# Revit family: Hager-UNIVERS-Surface_mounted-IP44-With_Cover-Without_DIN-Hosted-AT-de
name_source: partatom
category: Electrical Equipment
units: mm (PartAtom-declared; Revit-internal decimal feet)

## family parameters
Cut with Voids When Loaded = No
Host = Face
Maintain Annotation Orientation = Yes
Panel Configuration = Two Columns, Circuits Across
Part Type = Panelboard
Room Calculation Point = No
Round Connector Dimension = Use Diameter
Shared = No

## types (20) — shared parameters
BC_MODEL_ID = 1539154
BC_OBJECT_ID = 512277
BC_OBJECT_VERSION = #6
Code hager = ADD-EC000214_EU
EF000003 - Montageart = Aufputz
EF000007 - Farbe = weiß
EF000024 - UV-beständig = No
EF000049 - Tiefe = 161 mm  [stored 0.528215 ft]
EF000116 - RAL-Nummer = 9010
EF000118 - Mit Montageplatte = No
EF001062 - EMV-Ausführung = No
EF001088 - Anbaumöglichkeit = Yes
EF001134 - DIN-Schiene = No
EF004462 - Art der Schließung = sonstige
EF005474 - Schutzart (IP) = IP44
EF006244 - Transparenter Deckel/Tür = No
EF006306 - Mit Schloss = No
EF009212 - Ausführung Deckel = mit Ausschnitt
EF015776 - Erdungsklemmenblock = No
EF015777 - Neutralleiterklemmenblock = No
EF015941 - Signaldurchlassende Tür = No
ETIM class code = EC000214
ETIM class name = Small distribution board
HG000002-Mit tür = Yes
HG000003-Bereich = UNIVERS
HG000005-Dicke = 2 mm  [stored 0.00656168 ft]
HG000006-Unterputz = No
HG000011-Leere Reihen von unten = No
HG000012-Türschwenkwinkel = 90.00°
HG000013-Tür links = No
HG000014-Tür rechts = Yes
HG000015-Sichtbarkeit der Türöffnung = Yes
HG000016-3D-Türsichtbarkeit = Yes
HG000017-Distanz zwischen den Polen = 18 mm  [stored 0.0590551 ft]
HG000060-RAL-number = 9010
HG000099-Onfly Template ID-de-AT = 507532
Manufacturer = Hager
Name = UNIVERS-Surface_mounted-IP44-With_Cover-Without_DIN-AT
Name BIM&CO = Electricity
Name hager = ADD_Enclosures_EC000214
Uniformat = Low Tension Service & Dist.
Uniformat code = D501001
zero-valued in all types: Default Elevation, EF001131 - Innentiefe, HG000007-Anzahl der leeren Spalten, HG000008-Anzahl der leeren Reihen

## per-type parameters (varying)
| type | BC_VARIANT_ID | EF000008 - Breite | EF000040 - Höhe | EF000218 - Einbautiefe | EF000266 - Anzahl der Reihen | EF000332 - Einbauhöhe | EF000846 - Einbaubreite | EF002950 - Breite in Teilungseinheiten | HG000001-Anzahl der Spalten | HG000004-Herstellerreferenz | HG000009-Doppelflügeligen Tür | HG000010-Asymmetrische Türen | HGEF000266-Anzahl der Reihen | HGEF0002950-Breite in Teilungseinheiten |
| UNIVERS-Surface_mounted_W300_H500_D161_12_Modular_Spacing-FWQ31P | 1169533 | 300 mm | 500 mm  [stored 1.64042 ft] | 0 mm  [stored 0 ft] | 3 | 500 mm  [stored 1.64042 ft] | 300 mm | 12 | 1 | FWQ31P | No | No | 3 | 12 |
| UNIVERS-Surface_mounted_W550_H500_D161_24_Modular_Spacing-FWQ32P | 1169534 | 550 mm | 500 mm  [stored 1.64042 ft] | 161 mm  [stored 0.528215 ft] | 3 | 500 mm  [stored 1.64042 ft] | 550 mm | 24 | 2 | FWQ32P | No | No | 3 | 24 |
| UNIVERS-Surface_mounted_W800_H500_D161_36_Modular_Spacing-FWQ33P | 1169537 | 800 mm  [stored 2.62467 ft] | 500 mm  [stored 1.64042 ft] | 0 mm  [stored 0 ft] | 3 | 500 mm  [stored 1.64042 ft] | 800 mm  [stored 2.62467 ft] | 36 | 3 | FWQ33P | Yes | Yes | 3 | 36 |
| UNIVERS-Surface_mounted_W1050_H500_D161_48_Modular_Spacing-FWQ34P | 1169542 | 1050 mm | 500 mm  [stored 1.64042 ft] | 0 mm  [stored 0 ft] | 3 | 500 mm  [stored 1.64042 ft] | 1050 mm | 48 | 4 | FWQ34P | Yes | No | 3 | 48 |
| UNIVERS-Surface_mounted_W300_H650_D161_12_Modular_Spacing-FWQ41P | 1169548 | 300 mm | 650 mm  [stored 2.13255 ft] | 0 mm  [stored 0 ft] | 4 | 650 mm  [stored 2.13255 ft] | 300 mm | 12 | 1 | FWQ41P | No | No | 4 | 12 |
| UNIVERS-Surface_mounted_W550_H650_D161_24_Modular_Spacing-FWQ42P | 1169552 | 550 mm | 650 mm  [stored 2.13255 ft] | 0 mm  [stored 0 ft] | 4 | 650 mm  [stored 2.13255 ft] | 550 mm | 24 | 2 | FWQ42P | No | No | 4 | 24 |
| UNIVERS-Surface_mounted_W800_H650_D161_36_Modular_Spacing-FWQ43P | 1169555 | 800 mm  [stored 2.62467 ft] | 650 mm  [stored 2.13255 ft] | 0 mm  [stored 0 ft] | 4 | 650 mm  [stored 2.13255 ft] | 800 mm  [stored 2.62467 ft] | 36 | 3 | FWQ43P | Yes | Yes | 4 | 36 |
| UNIVERS-Surface_mounted_W1050_H650_D161_48_Modular_Spacing-FWQ44P | 1169557 | 1050 mm | 650 mm  [stored 2.13255 ft] | 0 mm  [stored 0 ft] | 4 | 650 mm  [stored 2.13255 ft] | 1050 mm | 48 | 4 | FWQ44P | Yes | No | 4 | 48 |
| UNIVERS-Surface_mounted_W300_H800_D161_12_Modular_Spacing-FWQ51P | 1169561 | 300 mm | 800 mm  [stored 2.62467 ft] | 0 mm  [stored 0 ft] | 5 | 800 mm  [stored 2.62467 ft] | 300 mm | 12 | 1 | FWQ51P | No | No | 5 | 12 |
| UNIVERS-Surface_mounted_W550_H800_D161_24_Modular_Spacing-FWQ52P | 1169563 | 550 mm | 800 mm  [stored 2.62467 ft] | 161 mm  [stored 0.528215 ft] | 5 | 800 mm  [stored 2.62467 ft] | 550 mm | 24 | 2 | FWQ52P | No | No | 5 | 24 |
| UNIVERS-Surface_mounted_W800_H800_D161_36_Modular_Spacing-FWQ53P | 1169566 | 800 mm  [stored 2.62467 ft] | 800 mm  [stored 2.62467 ft] | 0 mm  [stored 0 ft] | 5 | 800 mm  [stored 2.62467 ft] | 800 mm  [stored 2.62467 ft] | 36 | 3 | FWQ53P | Yes | Yes | 5 | 36 |
| UNIVERS-Surface_mounted_W1050_H800_D161_48_Modular_Spacing-FWQ54P | 1169570 | 1050 mm | 800 mm  [stored 2.62467 ft] | 0 mm  [stored 0 ft] | 5 | 800 mm  [stored 2.62467 ft] | 1050 mm | 48 | 4 | FWQ54P | Yes | No | 5 | 48 |
| UNIVERS-Surface_mounted_W300_H950_D161_12_Modular_Spacing-FWQ61P | 1169572 | 300 mm | 950 mm  [stored 3.1168 ft] | 0 mm  [stored 0 ft] | 6 | 950 mm  [stored 3.1168 ft] | 300 mm | 12 | 1 | FWQ61P | No | No | 6 | 12 |
| UNIVERS-Surface_mounted_W550_H950_D161_24_Modular_Spacing-FWQ62P | 1169575 | 550 mm | 950 mm  [stored 3.1168 ft] | 161 mm  [stored 0.528215 ft] | 6 | 950 mm  [stored 3.1168 ft] | 550 mm | 24 | 2 | FWQ62P | No | No | 6 | 24 |
| UNIVERS-Surface_mounted_W800_H950_D161_36_Modular_Spacing-FWQ63P | 1169578 | 800 mm  [stored 2.62467 ft] | 950 mm  [stored 3.1168 ft] | 0 mm  [stored 0 ft] | 6 | 950 mm  [stored 3.1168 ft] | 800 mm  [stored 2.62467 ft] | 36 | 3 | FWQ63P | Yes | Yes | 6 | 36 |
| UNIVERS-Surface_mounted_W1050_H950_D161_48_Modular_Spacing-FWQ64P | 1169581 | 1050 mm | 950 mm  [stored 3.1168 ft] | 161 mm  [stored 0.528215 ft] | 6 | 950 mm  [stored 3.1168 ft] | 1050 mm | 48 | 4 | FWQ64P | Yes | No | 6 | 48 |
| UNIVERS-Surface_mounted_W300_H1100_D161_12_Modular_Spacing-FWQ71P | 1169583 | 300 mm | 1100 mm  [stored 3.60892 ft] | 161 mm  [stored 0.528215 ft] | 7 | 1100 mm  [stored 3.60892 ft] | 300 mm | 12 | 1 | FWQ71P | No | No | 7 | 12 |
| UNIVERS-Surface_mounted_W550_H1100_D161_12_Modular_Spacing-FWQ72P | 1169588 | 550 mm | 1100 mm  [stored 3.60892 ft] | 0 mm  [stored 0 ft] | 7 | 1100 mm  [stored 3.60892 ft] | 550 mm | 12 | 2 | FWQ72P | No | No | 7 | 12 |
| UNIVERS-Surface_mounted_W800_H1100_D161_12_Modular_Spacing-FWQ73P | 1169591 | 800 mm  [stored 2.62467 ft] | 1100 mm  [stored 3.60892 ft] | 161 mm  [stored 0.528215 ft] | 7 | 1100 mm  [stored 3.60892 ft] | 800 mm  [stored 2.62467 ft] | 12 | 3 | FWQ73P | Yes | Yes | 7 | 12 |
| UNIVERS-Surface_mounted_W1050_H1100_D161_12_Modular_Spacing-FWQ74P | 1169594 | 1050 mm | 1100 mm  [stored 3.60892 ft] | 161 mm  [stored 0.528215 ft] | 7 | 1100 mm  [stored 3.60892 ft] | 1050 mm | 12 | 4 | FWQ74P | Yes | No | 7 | 12 |

note: column(s) folded — value = type name in every type: Reference

note: [stored X ft] marks values corroborated as IEEE doubles in the binary element streams (Revit-internal decimal feet)

## geometry (parser evidence)
native form markers: Sweep x17
no freeform markers — native parametric forms only
